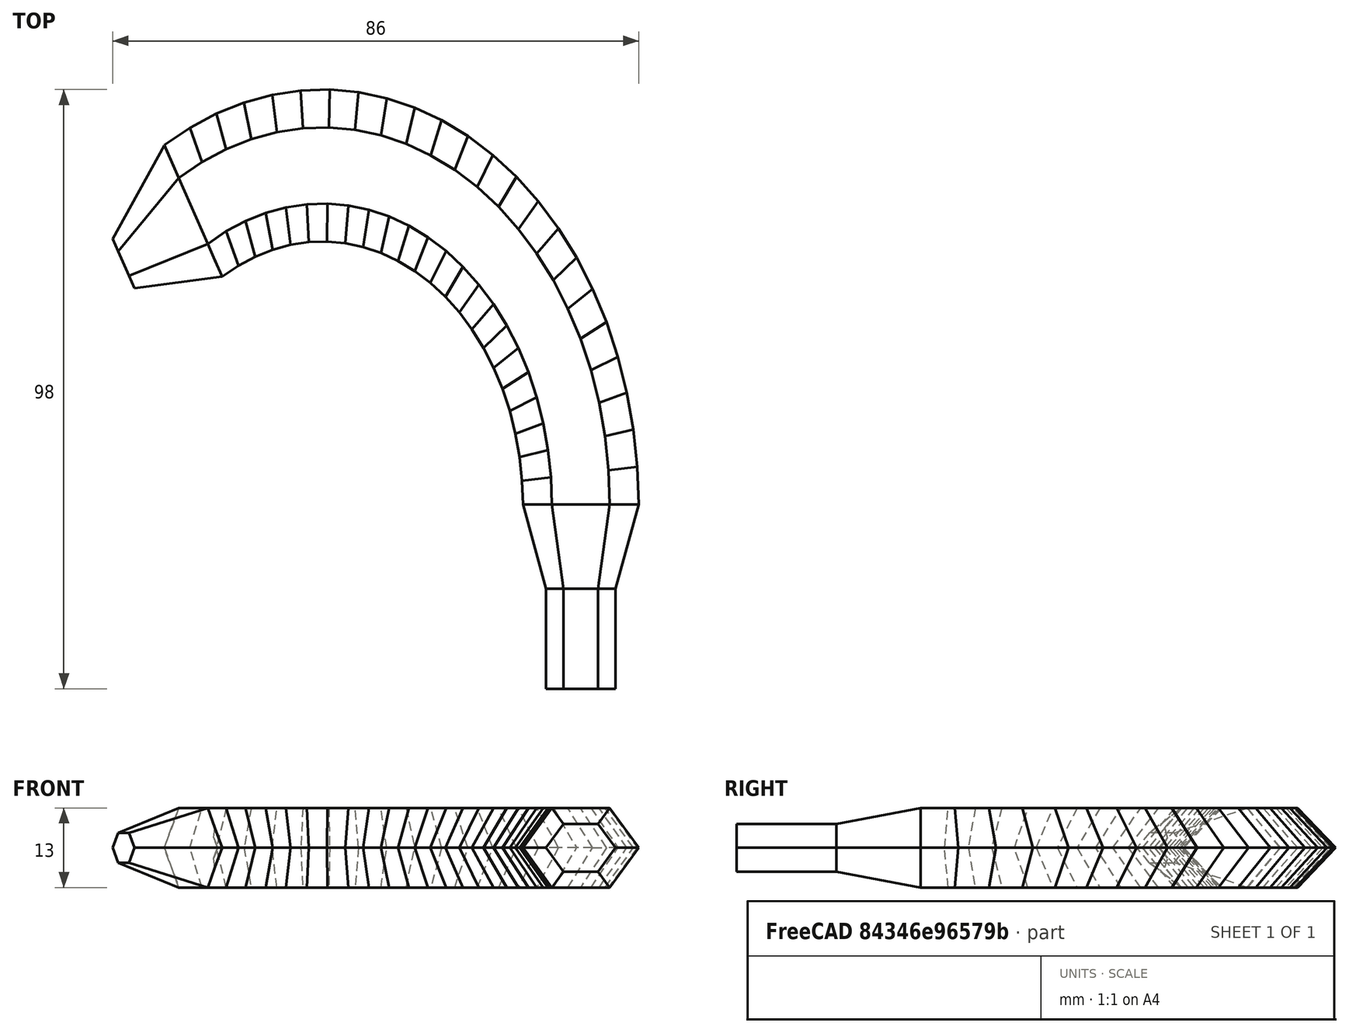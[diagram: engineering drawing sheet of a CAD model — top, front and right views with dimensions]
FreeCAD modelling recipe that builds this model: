
FCSTD DOCUMENT  (FreeCAD 0.20R29177 +426 (Git))
Label: banana
License: All rights reserved
LicenseURL: http://en.wikipedia.org/wiki/All_rights_reserved
objects: Part::Feature×2, Mesh::Feature×1, Part::Refine×1, PartDesign::FeatureBase×1, PartDesign::CoordinateSystem×1, PartDesign::Body×1
note: 6 computed .brp shape members not serialized (recipe doc carries the construction recipe); baked Part::Feature solids carry a one-line shape summary decoded from their .brp

FEATURE [Mesh::Feature] banana
FEATURE [Part::Feature] banana001
  shape: bbox 86 x 98 x 13 mm, 400 faces, 0 solids (baked)
FEATURE [Part::Refine] banana001001
  Source = -> banana001
FEATURE [Part::Feature] banana001001_solid  label="banana001001 (Solid)"
  shape: bbox 86 x 98 x 13 mm, 284 faces (baked)
FEATURE [PartDesign::FeatureBase] BaseFeature
  BaseFeature = -> banana001001_solid
FEATURE [PartDesign::CoordinateSystem] LCS_1
  AttacherType = Attacher::AttachEngine3D
FEATURE [PartDesign::Body] Body  label="Banana_Body"
  BaseFeature = -> banana001001_solid
  Group = -> [BaseFeature,LCS_1]
  Origin = -> Origin
  Tip = -> BaseFeature
